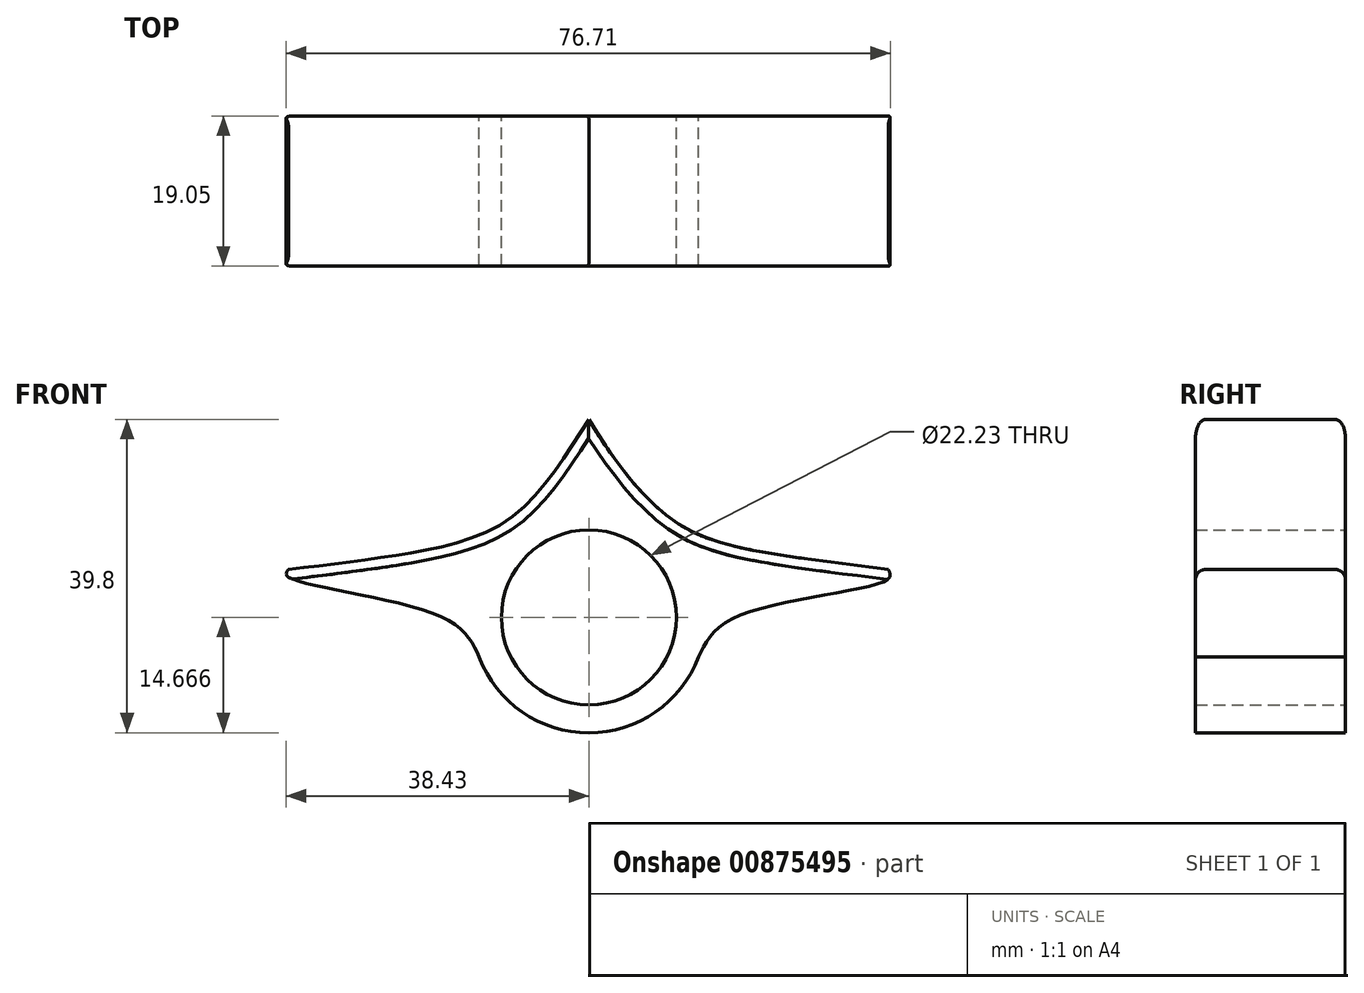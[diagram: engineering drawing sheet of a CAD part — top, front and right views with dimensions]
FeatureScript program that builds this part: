
annotation { "Feature Type Name" : "Feature", "Feature Type Description" : "" }
export const myFeature = defineFeature(function(context is Context, id is Id, definition is map)
    precondition{}
    {
        {
            var Q0;
            Q0=qCreatedBy(makeId("Front.planeOp"),FACE);
            var sketch = newSketch(context, id + "F0", { "sketchPlane" : qUnion([Q0])});
            skFitSpline(sketch, "E0", {"points": [v(-38.16, 0) * mm, v(-8.75, 7.48) * mm, v(0, 19.05) * mm], "startDerivative": vector(93.71, 11.15) * mm, "endDerivative": vector(20.19, 31.47) * mm});
            skFitSpline(sketch, "E1", {"points": [v(38.04, 0) * mm, v(9.6, 7.08) * mm, v(0, 19.05) * mm], "startDerivative": vector(-91.94, 11.59) * mm, "endDerivative": vector(-17.37, 29.3) * mm});
            skPoint(sketch, "E2.startSnap0", {"position": v(0, -11.11) * mm});
            skPoint(sketch, "E2.endSnap0", {"position": v(0, -11.11) * mm});
            skCircle(sketch, "E3", {"center": v(0, -6.08) * mm, "radius": 11.12 * mm});
            skArc(sketch, "E4", {"start": v(-13.92, -11.11) * mm, "mid": v(0, -20.75) * mm, "end": v(13.92, -11.11) * mm});
            skFitSpline(sketch, "E5", {"points": [v(13.92, -11.11) * mm, v(19.05, -5.88) * mm, v(38.04, -1.2) * mm, v(38.04, 0) * mm], "startDerivative": vector(8.24, 17.48) * mm, "endDerivative": vector(-4.7, 9.28) * mm});
            skFitSpline(sketch, "E6", {"points": [v(-13.92, -11.11) * mm, v(-19.05, -5.88) * mm, v(-38.3, -0.84) * mm, v(-38.16, 0) * mm], "startDerivative": vector(-7.84, 16.9) * mm, "endDerivative": vector(5.4, 7.4) * mm});
            skSolve(sketch);
        }
        {
            var Q0;
            Q0=makeQuery(id+"F0.imprint","IMPRINT",FACE,{"disambiguationData":[TD([[makeQuery(id+"F0.imprint","IMPRINT",EDGE,{"derivedFrom":sQuery(id+"F0.wireOp",EDGE,"E0")}),-1.0]])]});
            extrude(context, id + "F1", {"entities" : qUnion([Q0]), "depth" : 19.05 * mm, "offsetDistance" : 25.4 * mm});
        }
        {
            var Q0;
            Q0=makeQuery(id+"F1.opExtrude","CAP_EDGE",EDGE,{"disambiguationData":[OSD([sQuery(id+"F0.wireOp",EDGE,"E1")])],"isStart":false});
            var Q1;
            Q1=makeQuery(id+"F1.opExtrude","CAP_EDGE",EDGE,{"disambiguationData":[OSD([sQuery(id+"F0.wireOp",EDGE,"E1")])],"isStart":true});
            var Q2;
            Q2=makeQuery(id+"F1.opExtrude","CAP_EDGE",EDGE,{"disambiguationData":[OSD([sQuery(id+"F0.wireOp",EDGE,"E0")])],"isStart":false});
            var Q3;
            Q3=makeQuery(id+"F1.opExtrude","CAP_EDGE",EDGE,{"disambiguationData":[OSD([sQuery(id+"F0.wireOp",EDGE,"E0")])],"isStart":true});
            fillet(context, id + "F2", {"entities" : qUnion([Q0, Q1, Q2, Q3]), "radius" : 1.27 * mm, "tangentPropagation" : true, "allowEdgeOverflow" : false});
        }
    });
